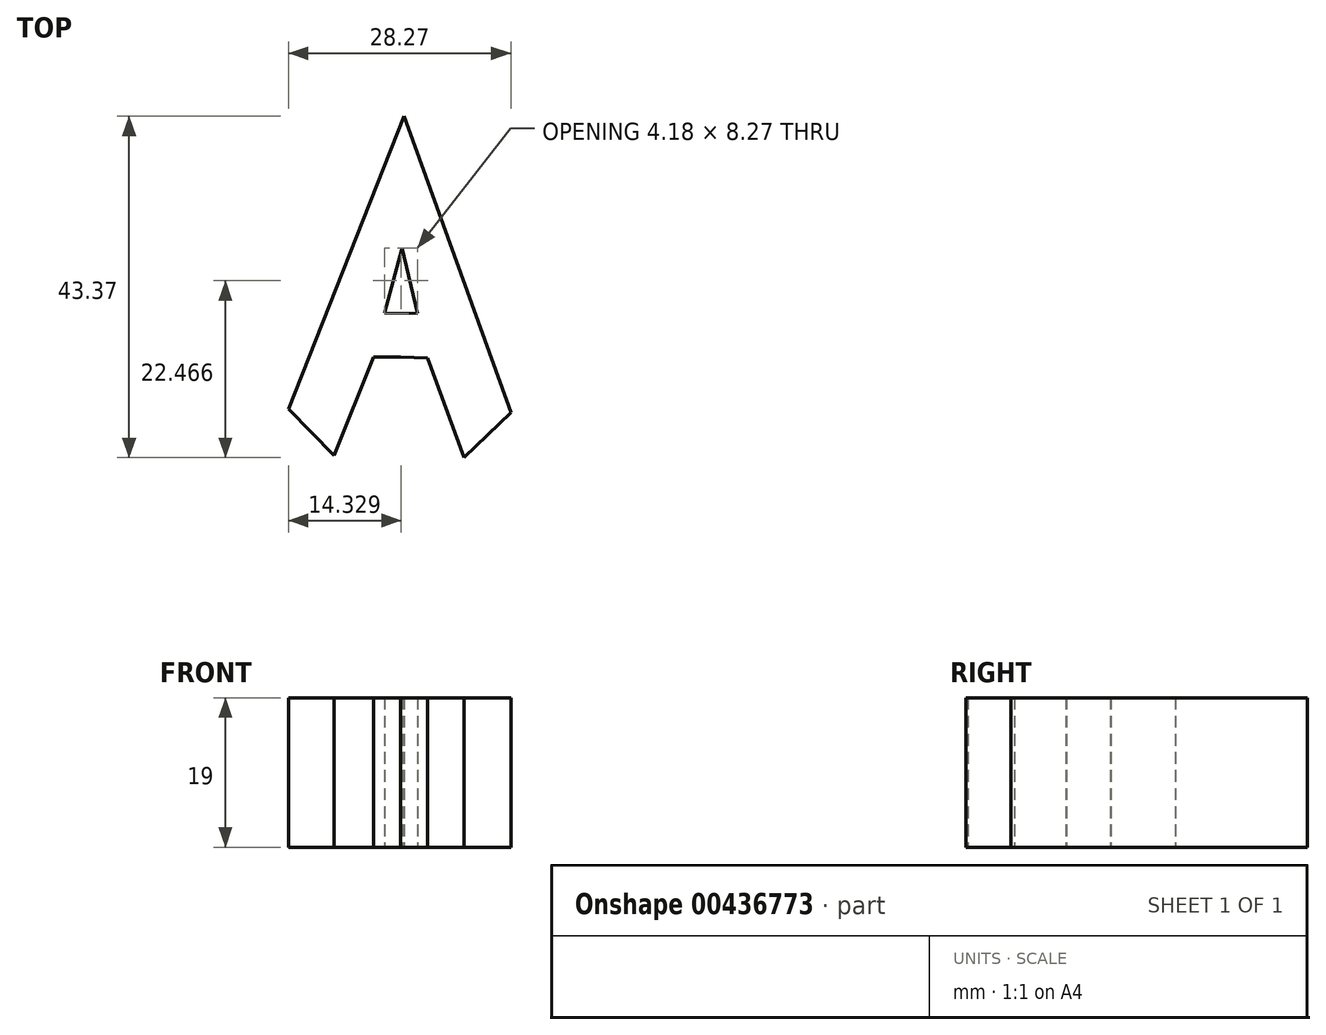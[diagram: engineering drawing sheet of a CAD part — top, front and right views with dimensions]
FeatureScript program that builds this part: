
annotation { "Feature Type Name" : "Feature", "Feature Type Description" : "" }
export const myFeature = defineFeature(function(context is Context, id is Id, definition is map)
    precondition{}
    {
        {
            var Q0;
            Q0=qCreatedBy(makeId("Top.planeOp"),FACE);
            var sketch = newSketch(context, id + "F0", { "sketchPlane" : qUnion([Q0])});
            skLineSegment(sketch, "E0", {"start": v(0, 0) * mm, "end": v(14.72, 37.2) * mm});
            skLineSegment(sketch, "E1", {"start": v(14.24, 6.6) * mm, "end": v(10.8, 6.6) * mm});
            skLineSegment(sketch, "E2", {"start": v(10.8, 6.6) * mm, "end": v(5.8, -5.93) * mm});
            skLineSegment(sketch, "E3", {"start": v(5.8, -5.93) * mm, "end": v(0, 0) * mm});
            skLineSegment(sketch, "E4", {"start": v(14.33, 12.22) * mm, "end": v(12.24, 12.22) * mm});
            skLineSegment(sketch, "E5", {"start": v(12.24, 12.22) * mm, "end": v(14.46, 20.42) * mm});
            skLineSegment(sketch, "E6", {"start": v(14.72, 37.2) * mm, "end": v(13.35, -50.53) * mm});
            skPoint(sketch, "E6.endSnap0", {"position": v(13.35, 16.32) * mm});
            skPoint(sketch, "E7.end.orphan", {"position": v(27.58, -5.93) * mm});
            skPoint(sketch, "E7.start.orphan", {"position": v(31.7, 0) * mm});
            skPoint(sketch, "E8.MirrorP", {"position": v(15.44, 16.29) * mm});
            skLineSegment(sketch, "E9.MirrorCS", {"start": v(28.27, -0.44) * mm, "end": v(14.72, 37.2) * mm});
            skLineSegment(sketch, "E10.MirrorCS", {"start": v(16.42, 12.15) * mm, "end": v(14.46, 20.42) * mm});
            skLineSegment(sketch, "E11.MirrorCS", {"start": v(14.24, 6.6) * mm, "end": v(17.68, 6.5) * mm});
            skLineSegment(sketch, "E12.MirrorCS", {"start": v(17.68, 6.5) * mm, "end": v(22.28, -6.18) * mm});
            skLineSegment(sketch, "E13.MirrorCS", {"start": v(22.28, -6.18) * mm, "end": v(28.27, -0.44) * mm});
            skLineSegment(sketch, "E14", {"start": v(12.24, 12.22) * mm, "end": v(16.42, 12.15) * mm});
            skSolve(sketch);
        }
        {
            var Q0;
            Q0 = qSketchRegion(id + "F0", true);
            extrude(context, id + "F1", {"entities" : qUnion([Q0]), "depth" : 19 * mm});
        }
    });
